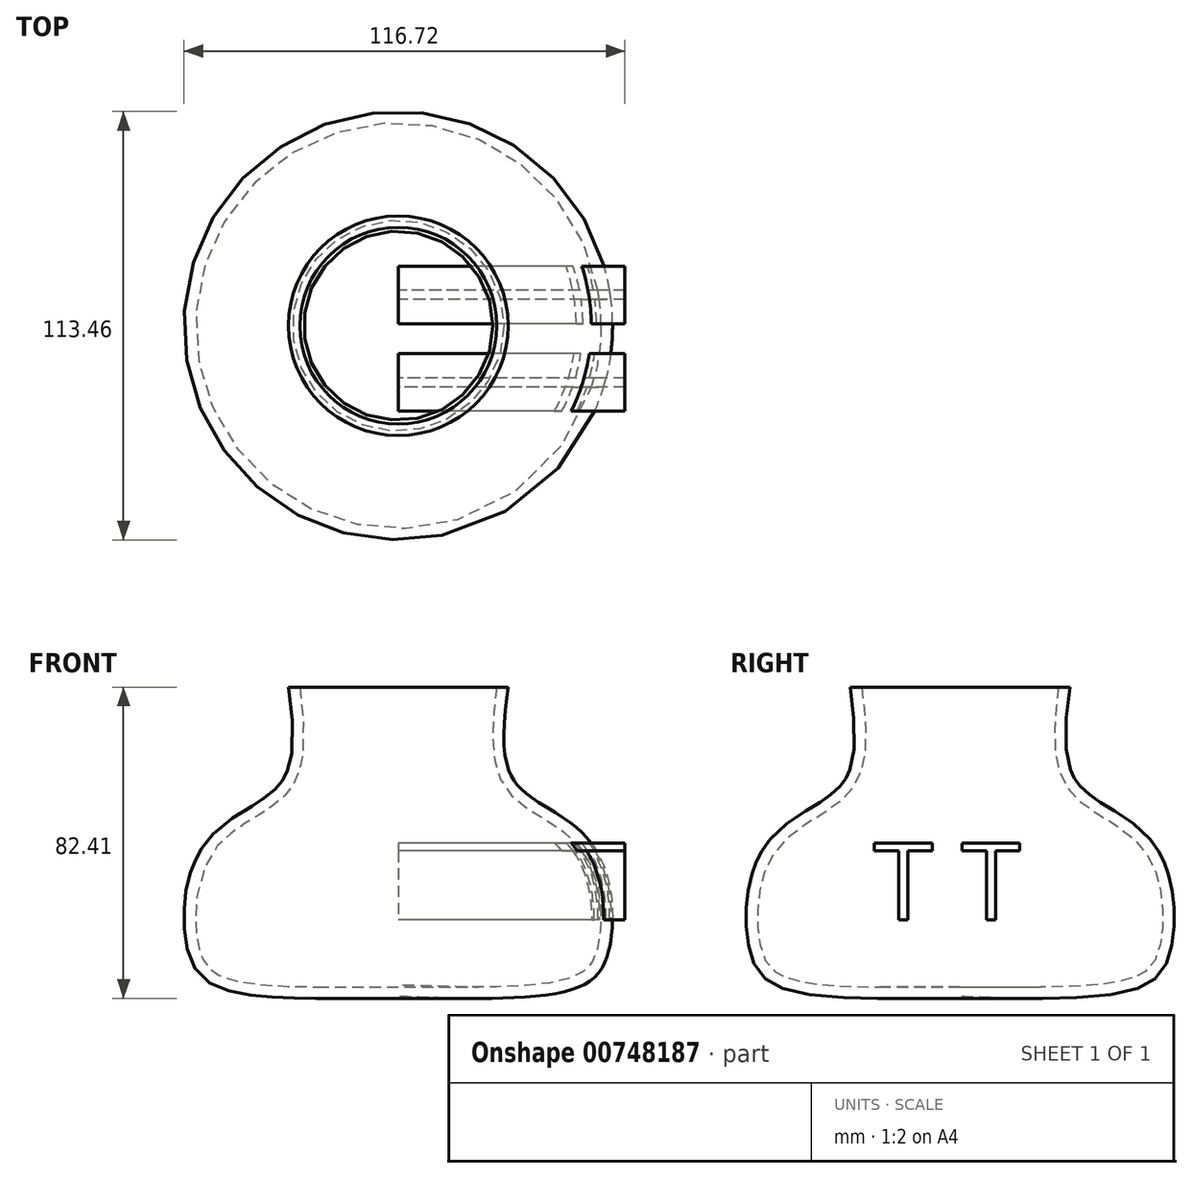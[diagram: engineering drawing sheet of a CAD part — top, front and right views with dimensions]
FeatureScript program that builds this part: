
annotation { "Feature Type Name" : "Feature", "Feature Type Description" : "" }
export const myFeature = defineFeature(function(context is Context, id is Id, definition is map)
    precondition{}
    {
        {
            var Q0;
            Q0=qCreatedBy(makeId("Front.planeOp"),FACE);
            var sketch = newSketch(context, id + "F0", { "sketchPlane" : qUnion([Q0])});
            skFitSpline(sketch, "E0", {"points": [v(26.54, 37.57) * mm, v(28.44, 7.13) * mm, v(48.6, -9.04) * mm, v(52.98, -34.33) * mm, v(46.13, -42.9) * mm, v(0, -44.99) * mm], "startDerivative": vector(-21.85, -163.58) * mm, "endDerivative": vector(-213.77, 6.66) * mm});
            skLineSegment(sketch, "E1", {"start": v(0, 48.03) * mm, "end": v(0, -56.78) * mm});
            skFitSpline(sketch, "E2.0", {"points": [v(29.5, 37.17) * mm, v(29.05, 33.76) * mm, v(28.38, 28.71) * mm, v(27.98, 22.47) * mm, v(28.03, 18.16) * mm, v(28.45, 14.96) * mm, v(29.03, 12.69) * mm, v(29.59, 11.14) * mm, v(30.17, 9.98) * mm, v(30.7, 9.12) * mm, v(31.28, 8.32) * mm, v(32.13, 7.34) * mm, v(33.36, 6.2) * mm, v(34.76, 5.1) * mm, v(36.84, 3.65) * mm, v(39.75, 1.85) * mm, v(42.86, -0.07) * mm, v(45.34, -1.8) * mm, v(47.15, -3.2) * mm, v(48.9, -4.78) * mm, v(50.25, -6.26) * mm, v(51.25, -7.55) * mm, v(52.17, -8.9) * mm, v(53.18, -10.67) * mm, v(54.18, -12.9) * mm, v(55.26, -15.95) * mm, v(56.17, -19.9) * mm, v(56.68, -24.63) * mm, v(56.69, -28.4) * mm, v(56.48, -31.24) * mm, v(56.28, -32.92) * mm, v(56.06, -34.2) * mm, v(55.82, -35.42) * mm, v(55.46, -36.88) * mm, v(54.89, -38.53) * mm, v(54.14, -40.09) * mm, v(53.2, -41.53) * mm, v(52.03, -42.82) * mm, v(50.67, -43.94) * mm, v(49.14, -44.87) * mm, v(47.45, -45.63) * mm, v(45, -46.47) * mm, v(41.54, -47.25) * mm, v(36.8, -47.88) * mm, v(31.5, -48.25) * mm, v(25.75, -48.43) * mm, v(19.61, -48.46) * mm, v(11.06, -48.33) * mm, v(4.36, -48.12) * mm, v(-0.1, -47.98) * mm]});
            skLineSegment(sketch, "E3", {"start": v(21.2, 33.95) * mm, "end": v(37.38, 33.95) * mm});
            skSolve(sketch);
        }
        {
            var Q0;
            {var subQ0=sQuery(id+"F0.wireOp",EDGE,"E1");var subQ1=sQuery(id+"F0.wireOp",EDGE,"E0");var subQ2=makeQuery(id+"F0.imprint","INTERSECT",VERTEX,{"derivedFrom":[subQ1,subQ0]});Q0=makeQuery(id+"F0.imprint","IMPRINT",FACE,{"disambiguationData":[TD([[makeQuery(id+"F0.imprint","IMPRINT",EDGE,{"disambiguationData":[TD([[subQ2,1.0]])],"derivedFrom":subQ1}),1.0]])]});}
            var Q1;
            Q1=sQuery(id+"F0.wireOp",EDGE,"E1");
            revolve(context, id + "F1", {"surfaceOperationType" : NewSurfaceOperationType.NEW, "entities" : qUnion([Q0]), "axis" : qUnion([Q1]), "revolveType" : RevolveType.FULL});
        }
        {
            var Q0;
            Q0=qCreatedBy(makeId("Right.planeOp"),FACE);
            var sketch = newSketch(context, id + "F2", { "sketchPlane" : qUnion([Q0])});
            skText(sketch, "E4", { "text": "T T", "fontName": "OpenSans-Regular.ttf"});
            const initialGuessF2  = {"E4": [-0.02292, -0.02768, 1, 0, 0.02054]};
            skSetInitialGuess(sketch, initialGuessF2);
            skSolve(sketch);
        }
        {
            var Q0;
            Q0 = qSketchRegion(id + "F2", true);
            extrude(context, id + "F3", {"entities" : qUnion([Q0]), "operationType" : NewBodyOperationType.ADD, "depth" : 60 * mm, "offsetDistance" : 25 * mm});
        }
    });
